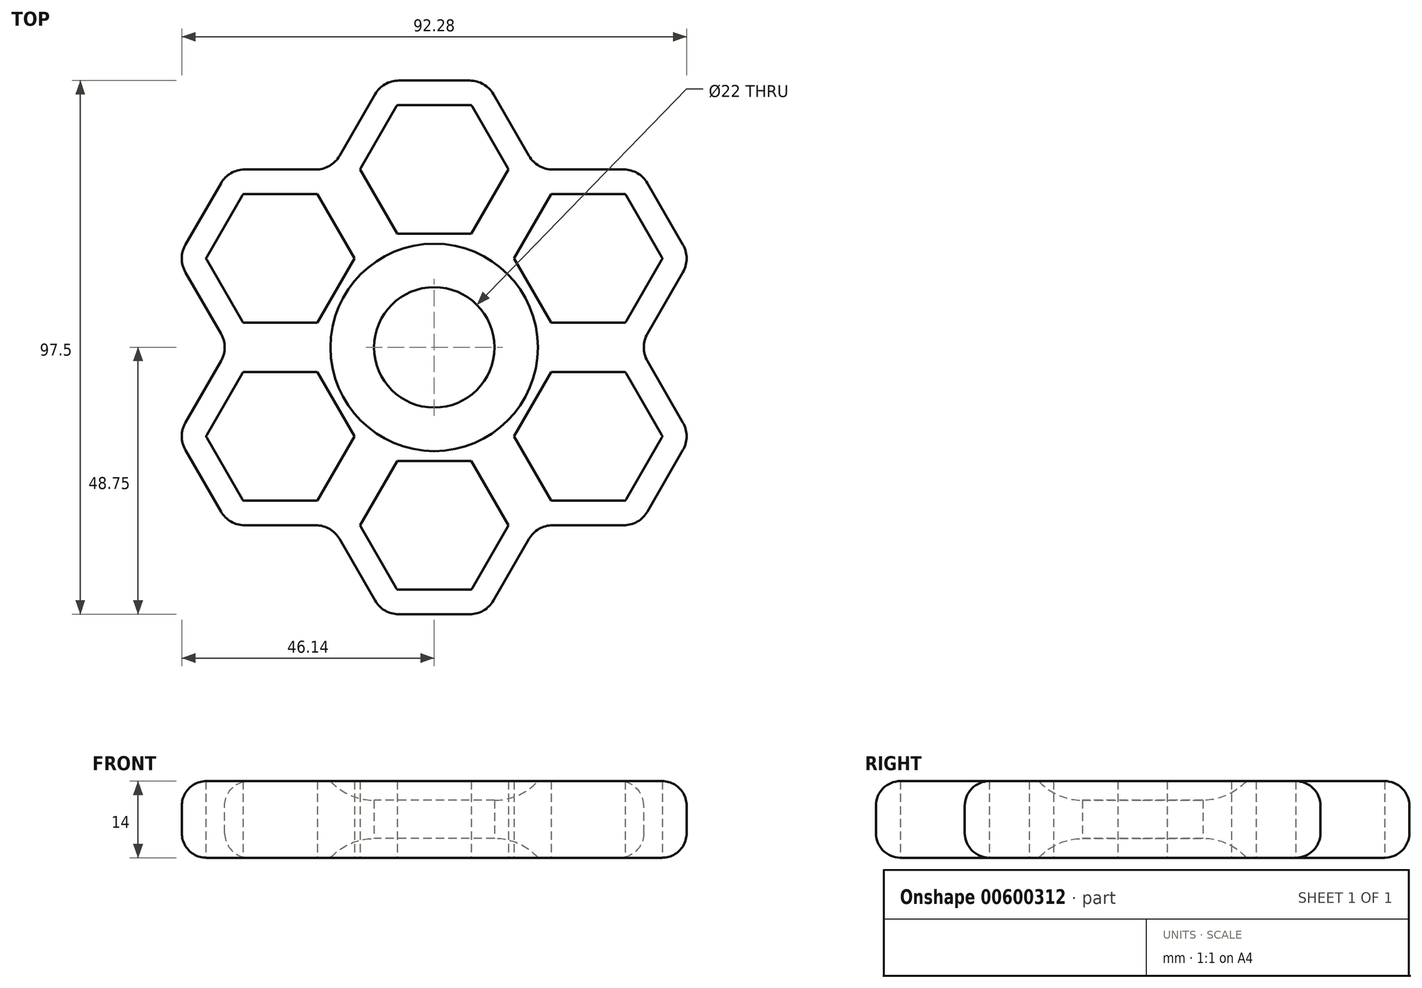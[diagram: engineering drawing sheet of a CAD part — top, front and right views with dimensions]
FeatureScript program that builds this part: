
annotation { "Feature Type Name" : "Feature", "Feature Type Description" : "" }
export const myFeature = defineFeature(function(context is Context, id is Id, definition is map)
    precondition{}
    {
        {
            var Q0;
            Q0=qCreatedBy(makeId("Top.planeOp"),FACE);
            var sketch = newSketch(context, id + "F0", { "sketchPlane" : qUnion([Q0])});
            skCircle(sketch, "E0", {"center": v(0, 0) * mm, "radius": 49.64 * mm, "construction": true});
            skCircle(sketch, "E1.cCircle", {"center": v(0, 32.5) * mm, "radius": 11.75 * mm, "construction": true});
            skLineSegment(sketch, "E1.0", {"start": v(6.78, 44.25) * mm, "end": v(13.57, 32.5) * mm});
            skLineSegment(sketch, "E1.1", {"start": v(13.57, 32.5) * mm, "end": v(6.78, 20.75) * mm});
            skLineSegment(sketch, "E1.2", {"start": v(6.78, 20.75) * mm, "end": v(-6.78, 20.75) * mm});
            skLineSegment(sketch, "E1.3", {"start": v(-6.78, 20.75) * mm, "end": v(-13.57, 32.5) * mm});
            skLineSegment(sketch, "E1.4", {"start": v(-13.57, 32.5) * mm, "end": v(-6.78, 44.25) * mm});
            skLineSegment(sketch, "E1.5", {"start": v(-6.78, 44.25) * mm, "end": v(6.78, 44.25) * mm});
            skPoint(sketch, "E1.0.midPoint", {"position": v(10.18, 38.38) * mm});
            skLineSegment(sketch, "E2", {"start": v(0, 0) * mm, "end": v(0, 32.5) * mm, "construction": true});
            skCircle(sketch, "E3.cCircle", {"center": v(0, 32.5) * mm, "radius": 16.25 * mm, "construction": true});
            skLineSegment(sketch, "E3.3", {"start": v(-18.76, 32.5) * mm, "end": v(-9.38, 48.75) * mm});
            skLineSegment(sketch, "E3.4", {"start": v(-9.38, 48.75) * mm, "end": v(9.38, 48.75) * mm});
            skLineSegment(sketch, "E3.5", {"start": v(9.38, 48.75) * mm, "end": v(18.76, 32.5) * mm});
            skPoint(sketch, "E3.0.midPoint", {"position": v(14.15, 24.5) * mm});
            skCircle(sketch, "E4.cCircle", {"center": v(28.15, 16.25) * mm, "radius": 11.75 * mm, "construction": true});
            skLineSegment(sketch, "E4.0", {"start": v(41.71, 16.25) * mm, "end": v(34.93, 4.5) * mm});
            skLineSegment(sketch, "E4.1", {"start": v(34.93, 4.5) * mm, "end": v(21.36, 4.5) * mm});
            skLineSegment(sketch, "E4.2", {"start": v(21.36, 4.5) * mm, "end": v(14.58, 16.25) * mm});
            skLineSegment(sketch, "E4.3", {"start": v(14.58, 16.25) * mm, "end": v(21.36, 28) * mm});
            skLineSegment(sketch, "E4.4", {"start": v(21.36, 28) * mm, "end": v(34.93, 28) * mm});
            skLineSegment(sketch, "E4.5", {"start": v(34.93, 28) * mm, "end": v(41.71, 16.25) * mm});
            skPoint(sketch, "E4.0.midPoint", {"position": v(38.32, 10.37) * mm});
            skCircle(sketch, "E5.cCircle", {"center": v(28.15, 16.25) * mm, "radius": 16.25 * mm, "construction": true});
            skLineSegment(sketch, "E5.3", {"start": v(18.76, 32.5) * mm, "end": v(37.53, 32.5) * mm});
            skLineSegment(sketch, "E5.4", {"start": v(37.53, 32.5) * mm, "end": v(46.9, 16.25) * mm});
            skLineSegment(sketch, "E5.5", {"start": v(46.9, 16.25) * mm, "end": v(37.53, 0) * mm});
            skPoint(sketch, "E5.0.midPoint", {"position": v(27.44, 0.02) * mm});
            skCircle(sketch, "E6.cCircle", {"center": v(28.15, -16.25) * mm, "radius": 11.75 * mm, "construction": true});
            skLineSegment(sketch, "E6.0", {"start": v(34.93, -28) * mm, "end": v(21.36, -28) * mm});
            skLineSegment(sketch, "E6.1", {"start": v(21.36, -28) * mm, "end": v(14.58, -16.25) * mm});
            skLineSegment(sketch, "E6.2", {"start": v(14.58, -16.25) * mm, "end": v(21.36, -4.5) * mm});
            skLineSegment(sketch, "E6.3", {"start": v(21.36, -4.5) * mm, "end": v(34.93, -4.5) * mm});
            skLineSegment(sketch, "E6.4", {"start": v(34.93, -4.5) * mm, "end": v(41.71, -16.25) * mm});
            skLineSegment(sketch, "E6.5", {"start": v(41.71, -16.25) * mm, "end": v(34.93, -28) * mm});
            skPoint(sketch, "E6.0.midPoint", {"position": v(28.15, -28) * mm});
            skCircle(sketch, "E7.cCircle", {"center": v(28.15, -16.25) * mm, "radius": 16.25 * mm, "construction": true});
            skLineSegment(sketch, "E7.3", {"start": v(37.53, 0) * mm, "end": v(46.9, -16.25) * mm});
            skLineSegment(sketch, "E7.4", {"start": v(46.9, -16.25) * mm, "end": v(37.53, -32.5) * mm});
            skLineSegment(sketch, "E7.5", {"start": v(37.53, -32.5) * mm, "end": v(18.76, -32.5) * mm});
            skPoint(sketch, "E7.0.midPoint", {"position": v(13.86, -24) * mm});
            skCircle(sketch, "E8.cCircle", {"center": v(0, -32.5) * mm, "radius": 11.75 * mm, "construction": true});
            skLineSegment(sketch, "E8.0", {"start": v(-6.78, -20.75) * mm, "end": v(6.78, -20.75) * mm});
            skLineSegment(sketch, "E8.1", {"start": v(6.78, -20.75) * mm, "end": v(13.57, -32.5) * mm});
            skLineSegment(sketch, "E8.2", {"start": v(13.57, -32.5) * mm, "end": v(6.78, -44.25) * mm});
            skLineSegment(sketch, "E8.3", {"start": v(6.78, -44.25) * mm, "end": v(-6.78, -44.25) * mm});
            skLineSegment(sketch, "E8.4", {"start": v(-6.78, -44.25) * mm, "end": v(-13.57, -32.5) * mm});
            skLineSegment(sketch, "E8.5", {"start": v(-13.57, -32.5) * mm, "end": v(-6.78, -20.75) * mm});
            skPoint(sketch, "E8.0.midPoint", {"position": v(0, -20.75) * mm});
            skCircle(sketch, "E9.cCircle", {"center": v(0, -32.5) * mm, "radius": 16.25 * mm, "construction": true});
            skLineSegment(sketch, "E9.1", {"start": v(18.76, -32.5) * mm, "end": v(9.38, -48.75) * mm});
            skLineSegment(sketch, "E9.2", {"start": v(9.38, -48.75) * mm, "end": v(-9.38, -48.75) * mm});
            skLineSegment(sketch, "E9.3", {"start": v(-9.38, -48.75) * mm, "end": v(-18.76, -32.5) * mm});
            skPoint(sketch, "E9.0.midPoint", {"position": v(14.28, -24.74) * mm});
            skCircle(sketch, "E10.cCircle", {"center": v(-28.15, 16.25) * mm, "radius": 11.75 * mm, "construction": true});
            skLineSegment(sketch, "E10.0", {"start": v(-41.71, 16.25) * mm, "end": v(-34.93, 28) * mm});
            skLineSegment(sketch, "E10.1", {"start": v(-34.93, 28) * mm, "end": v(-21.36, 28) * mm});
            skLineSegment(sketch, "E10.2", {"start": v(-21.36, 28) * mm, "end": v(-14.58, 16.25) * mm});
            skLineSegment(sketch, "E10.3", {"start": v(-14.58, 16.25) * mm, "end": v(-21.36, 4.5) * mm});
            skLineSegment(sketch, "E10.4", {"start": v(-21.36, 4.5) * mm, "end": v(-34.93, 4.5) * mm});
            skLineSegment(sketch, "E10.5", {"start": v(-34.93, 4.5) * mm, "end": v(-41.71, 16.25) * mm});
            skPoint(sketch, "E10.0.midPoint", {"position": v(-38.32, 22.13) * mm});
            skCircle(sketch, "E11.cCircle", {"center": v(-28.15, 16.25) * mm, "radius": 16.25 * mm, "construction": true});
            skLineSegment(sketch, "E11.0", {"start": v(-37.53, 32.5) * mm, "end": v(-18.76, 32.5) * mm});
            skLineSegment(sketch, "E11.4", {"start": v(-37.53, 0) * mm, "end": v(-46.9, 16.25) * mm});
            skLineSegment(sketch, "E11.5", {"start": v(-46.9, 16.25) * mm, "end": v(-37.53, 32.5) * mm});
            skPoint(sketch, "E11.0.midPoint", {"position": v(-28.15, 32.5) * mm});
            skCircle(sketch, "E12.cCircle", {"center": v(-28.15, -16.25) * mm, "radius": 11.75 * mm, "construction": true});
            skLineSegment(sketch, "E12.0", {"start": v(-34.93, -28) * mm, "end": v(-41.71, -16.25) * mm});
            skLineSegment(sketch, "E12.1", {"start": v(-41.71, -16.25) * mm, "end": v(-34.93, -4.5) * mm});
            skLineSegment(sketch, "E12.2", {"start": v(-34.93, -4.5) * mm, "end": v(-21.36, -4.5) * mm});
            skLineSegment(sketch, "E12.3", {"start": v(-21.36, -4.5) * mm, "end": v(-14.58, -16.25) * mm});
            skLineSegment(sketch, "E12.4", {"start": v(-14.58, -16.25) * mm, "end": v(-21.36, -28) * mm});
            skLineSegment(sketch, "E12.5", {"start": v(-21.36, -28) * mm, "end": v(-34.93, -28) * mm});
            skPoint(sketch, "E12.0.midPoint", {"position": v(-38.32, -22.12) * mm});
            skCircle(sketch, "E13.cCircle", {"center": v(-28.15, -16.25) * mm, "radius": 16.25 * mm, "construction": true});
            skLineSegment(sketch, "E13.0", {"start": v(-46.9, -16.25) * mm, "end": v(-37.53, 0) * mm});
            skLineSegment(sketch, "E13.4", {"start": v(-18.76, -32.5) * mm, "end": v(-37.53, -32.5) * mm});
            skLineSegment(sketch, "E13.5", {"start": v(-37.53, -32.5) * mm, "end": v(-46.9, -16.25) * mm});
            skPoint(sketch, "E13.0.midPoint", {"position": v(-42.22, -8.12) * mm});
            skSolve(sketch);
        }
        {
            var Q0;
            Q0=qCreatedBy(makeId("Top.planeOp"),FACE);
            var sketch = newSketch(context, id + "F1", { "sketchPlane" : qUnion([Q0])});
            skCircle(sketch, "E14", {"center": v(0, 0) * mm, "radius": 11 * mm});
            skSolve(sketch);
        }
        {
            var Q0;
            Q0 = qSketchRegion(id + "F0", true);
            extrude(context, id + "F2", {"entities" : qUnion([Q0]), "endBound" : BoundingType.SYMMETRIC, "depth" : 14 * mm, "offsetDistance" : 25 * mm});
        }
        {
            var Q0;
            Q0=makeQuery(id+"F2.opExtrude","SWEPT_EDGE",EDGE,{"disambiguationData":[OSD([sQuery(id+"F0.wireOp",EDGE,"E7.5"),sQuery(id+"F0.wireOp",EDGE,"E9.1")])]});
            var Q1;
            Q1=makeQuery(id+"F2.opExtrude","SWEPT_EDGE",EDGE,{"disambiguationData":[OSD([sQuery(id+"F0.wireOp",EDGE,"E9.1"),sQuery(id+"F0.wireOp",EDGE,"E9.2")])]});
            var Q2;
            Q2=makeQuery(id+"F2.opExtrude","SWEPT_EDGE",EDGE,{"disambiguationData":[OSD([sQuery(id+"F0.wireOp",EDGE,"E9.2"),sQuery(id+"F0.wireOp",EDGE,"E9.3")])]});
            var Q3;
            Q3=makeQuery(id+"F2.opExtrude","SWEPT_EDGE",EDGE,{"disambiguationData":[OSD([sQuery(id+"F0.wireOp",EDGE,"E13.4"),sQuery(id+"F0.wireOp",EDGE,"E13.5")])]});
            var Q4;
            Q4=makeQuery(id+"F2.opExtrude","SWEPT_EDGE",EDGE,{"disambiguationData":[OSD([sQuery(id+"F0.wireOp",EDGE,"E7.4"),sQuery(id+"F0.wireOp",EDGE,"E7.5")])]});
            var Q5;
            Q5=makeQuery(id+"F2.opExtrude","SWEPT_EDGE",EDGE,{"disambiguationData":[OSD([sQuery(id+"F0.wireOp",EDGE,"E7.3"),sQuery(id+"F0.wireOp",EDGE,"E7.4")])]});
            var Q6;
            Q6=makeQuery(id+"F2.opExtrude","SWEPT_EDGE",EDGE,{"disambiguationData":[OSD([sQuery(id+"F0.wireOp",EDGE,"E5.4"),sQuery(id+"F0.wireOp",EDGE,"E5.5")])]});
            var Q7;
            Q7=makeQuery(id+"F2.opExtrude","SWEPT_EDGE",EDGE,{"disambiguationData":[OSD([sQuery(id+"F0.wireOp",EDGE,"E9.3"),sQuery(id+"F0.wireOp",EDGE,"E13.4")])]});
            var Q8;
            Q8=makeQuery(id+"F2.opExtrude","SWEPT_EDGE",EDGE,{"disambiguationData":[OSD([sQuery(id+"F0.wireOp",EDGE,"E13.0"),sQuery(id+"F0.wireOp",EDGE,"E13.5")])]});
            var Q9;
            Q9=makeQuery(id+"F2.opExtrude","SWEPT_EDGE",EDGE,{"disambiguationData":[OSD([sQuery(id+"F0.wireOp",EDGE,"E11.4"),sQuery(id+"F0.wireOp",EDGE,"E13.0")])]});
            var Q10;
            Q10=makeQuery(id+"F2.opExtrude","SWEPT_EDGE",EDGE,{"disambiguationData":[OSD([sQuery(id+"F0.wireOp",EDGE,"E11.4"),sQuery(id+"F0.wireOp",EDGE,"E11.5")])]});
            var Q11;
            Q11=makeQuery(id+"F2.opExtrude","SWEPT_EDGE",EDGE,{"disambiguationData":[OSD([sQuery(id+"F0.wireOp",EDGE,"E11.0"),sQuery(id+"F0.wireOp",EDGE,"E11.5")])]});
            var Q12;
            Q12=makeQuery(id+"F2.opExtrude","SWEPT_EDGE",EDGE,{"disambiguationData":[OSD([sQuery(id+"F0.wireOp",EDGE,"E3.3"),sQuery(id+"F0.wireOp",EDGE,"E11.0")])]});
            var Q13;
            Q13=makeQuery(id+"F2.opExtrude","SWEPT_EDGE",EDGE,{"disambiguationData":[OSD([sQuery(id+"F0.wireOp",EDGE,"E3.3"),sQuery(id+"F0.wireOp",EDGE,"E3.4")])]});
            var Q14;
            Q14=makeQuery(id+"F2.opExtrude","SWEPT_EDGE",EDGE,{"disambiguationData":[OSD([sQuery(id+"F0.wireOp",EDGE,"E3.4"),sQuery(id+"F0.wireOp",EDGE,"E3.5")])]});
            var Q15;
            Q15=makeQuery(id+"F2.opExtrude","SWEPT_EDGE",EDGE,{"disambiguationData":[OSD([sQuery(id+"F0.wireOp",EDGE,"E3.5"),sQuery(id+"F0.wireOp",EDGE,"E5.3")])]});
            var Q16;
            Q16=makeQuery(id+"F2.opExtrude","SWEPT_EDGE",EDGE,{"disambiguationData":[OSD([sQuery(id+"F0.wireOp",EDGE,"E5.3"),sQuery(id+"F0.wireOp",EDGE,"E5.4")])]});
            var Q17;
            Q17=makeQuery(id+"F2.opExtrude","SWEPT_EDGE",EDGE,{"disambiguationData":[OSD([sQuery(id+"F0.wireOp",EDGE,"E5.5"),sQuery(id+"F0.wireOp",EDGE,"E7.3")])]});
            fillet(context, id + "F3", {"entities" : qUnion([Q0, Q1, Q2, Q3, Q4, Q5, Q6, Q7, Q8, Q9, Q10, Q11, Q12, Q13, Q14, Q15, Q16, Q17]), "radius" : 5 * mm, "tangentPropagation" : true, "allowEdgeOverflow" : false});
        }
        {
            var Q0;
            Q0=makeQuery(id+"F2.opExtrude","CAP_EDGE",EDGE,{"disambiguationData":[OSD([sQuery(id+"F0.wireOp",EDGE,"E13.5")])],"isStart":false});
            var Q1;
            Q1=makeQuery(id+"F2.opExtrude","CAP_EDGE",EDGE,{"disambiguationData":[OSD([sQuery(id+"F0.wireOp",EDGE,"E13.5")])],"isStart":true});
            fillet(context, id + "F4", {"entities" : qUnion([Q0, Q1]), "radius" : 4.5 * mm, "tangentPropagation" : true, "allowEdgeOverflow" : false});
        }
        {
            var Q0;
            Q0 = qSketchRegion(id + "F1", true);
            extrude(context, id + "F5", {"entities" : qUnion([Q0]), "operationType" : NewBodyOperationType.REMOVE, "endBound" : BoundingType.SYMMETRIC, "depth" : 25 * mm, "offsetDistance" : 25 * mm});
        }
        {
            var Q0;
            Q0=qCreatedBy(makeId("Right.planeOp"),FACE);
            var sketch = newSketch(context, id + "F6", { "sketchPlane" : qUnion([Q0])});
            skPoint(sketch, "E15.0", {"position": v(-20.75, 7) * mm});
            skLineSegment(sketch, "E16.0", {"start": v(11, 7) * mm, "end": v(-11, 7) * mm, "construction": true});
            skArc(sketch, "E17", {"start": v(-18.95, 7) * mm, "mid": v(-15.34, 4.41) * mm, "end": v(-11, 3.5) * mm});
            skLineSegment(sketch, "E18", {"start": v(-18.95, 7) * mm, "end": v(-11, 7) * mm});
            skLineSegment(sketch, "E19", {"start": v(-11, 3.5) * mm, "end": v(-11, 7) * mm});
            skLineSegment(sketch, "E20", {"start": v(-11, -3.5) * mm, "end": v(-11, -7) * mm});
            skLineSegment(sketch, "E21", {"start": v(-11, -7) * mm, "end": v(-18.95, -7) * mm});
            skArc(sketch, "E22", {"start": v(-11, -3.5) * mm, "mid": v(-15.34, -4.41) * mm, "end": v(-18.95, -7) * mm});
            skLineSegment(sketch, "E23", {"start": v(0, 0) * mm, "end": v(0, 14) * mm, "construction": true});
            skSolve(sketch);
        }
        {
            var Q0;
            Q0 = qSketchRegion(id + "F6", true);
            var Q1;
            Q1=sQuery(id+"F6.wireOp",EDGE,"E23");
            revolve(context, id + "F7", {"operationType" : NewBodyOperationType.REMOVE, "surfaceOperationType" : NewSurfaceOperationType.NEW, "entities" : qUnion([Q0]), "axis" : qUnion([Q1]), "revolveType" : RevolveType.FULL, "oppositeDirection" : true});
        }
    });
